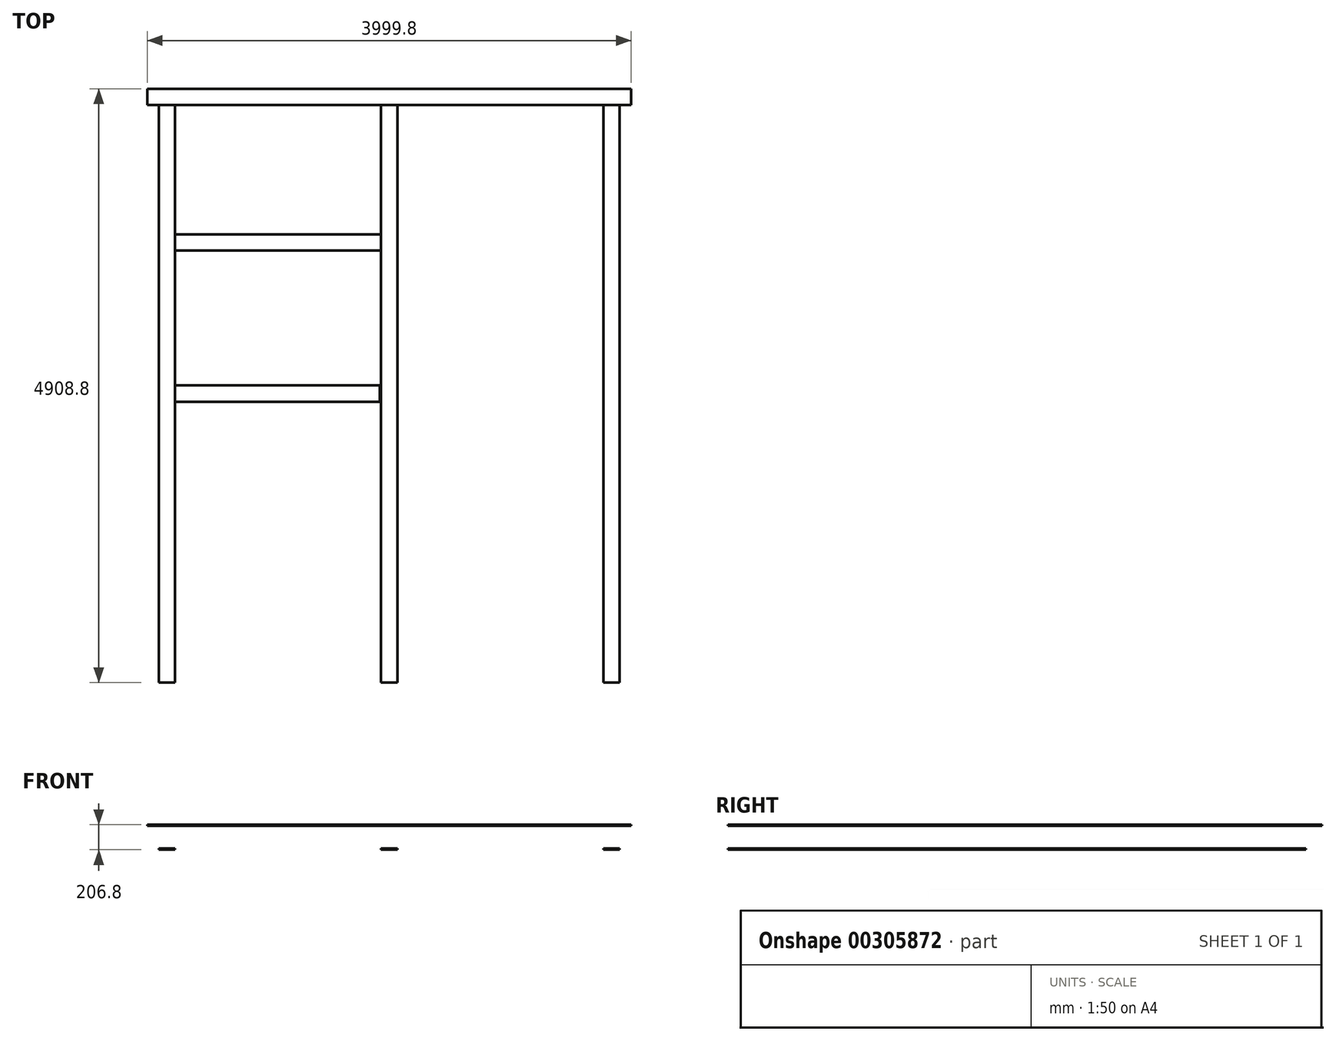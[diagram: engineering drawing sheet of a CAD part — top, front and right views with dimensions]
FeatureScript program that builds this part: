
annotation { "Feature Type Name" : "Feature", "Feature Type Description" : "" }
export const myFeature = defineFeature(function(context is Context, id is Id, definition is map)
    precondition{}
    {
        {
            var Q0;
            Q0=qCreatedBy(makeId("Front.planeOp"),FACE);
            var sketch = newSketch(context, id + "F0", { "sketchPlane" : qUnion([Q0])});
            skLineSegment(sketch, "E0", {"start": v(-1803, 76.08) * mm, "end": v(1869, 76.08) * mm, "construction": true});
            skLineSegment(sketch, "E1", {"start": v(33, 76.08) * mm, "end": v(33, -634.44) * mm, "construction": true});
            skLineSegment(sketch, "E2", {"start": v(-1803, 80.88) * mm, "end": v(1869, 80.88) * mm, "construction": true});
            skLineSegment(sketch, "E3", {"start": v(-1803, 278.08) * mm, "end": v(1869, 278.08) * mm, "construction": true});
            skLineSegment(sketch, "E4", {"start": v(-1803, 282.88) * mm, "end": v(1869, 282.88) * mm, "construction": true});
            skLineSegment(sketch, "E5", {"start": v(-1803, 282.88) * mm, "end": v(-1803, 76.08) * mm, "construction": true});
            skLineSegment(sketch, "E6", {"start": v(-1803, 179.48) * mm, "end": v(1869, 179.48) * mm, "construction": true});
            skLineSegment(sketch, "E7.bottom", {"start": v(-1869.9, 282.88) * mm, "end": v(-1736.1, 282.88) * mm});
            skLineSegment(sketch, "E7.top", {"start": v(-1869.9, 273.28) * mm, "end": v(-1736.1, 273.28) * mm});
            skLineSegment(sketch, "E7.left", {"start": v(-1869.9, 282.88) * mm, "end": v(-1869.9, 273.28) * mm});
            skLineSegment(sketch, "E7.right", {"start": v(-1736.1, 282.88) * mm, "end": v(-1736.1, 273.28) * mm});
            skPoint(sketch, "E7.middle", {"position": v(-1803, 278.08) * mm});
            skLineSegment(sketch, "E8.bottom", {"start": v(-1736.1, 76.08) * mm, "end": v(-1869.9, 76.08) * mm});
            skLineSegment(sketch, "E8.top", {"start": v(-1736.1, 85.68) * mm, "end": v(-1869.9, 85.68) * mm});
            skLineSegment(sketch, "E8.left", {"start": v(-1736.1, 76.08) * mm, "end": v(-1736.1, 85.68) * mm});
            skLineSegment(sketch, "E8.right", {"start": v(-1869.9, 76.08) * mm, "end": v(-1869.9, 85.68) * mm});
            skPoint(sketch, "E8.middle", {"position": v(-1803, 80.88) * mm});
            skLineSegment(sketch, "E9.bottom", {"start": v(-1799.85, 85.68) * mm, "end": v(-1806.15, 85.68) * mm});
            skLineSegment(sketch, "E9.top", {"start": v(-1799.85, 273.28) * mm, "end": v(-1806.15, 273.28) * mm});
            skLineSegment(sketch, "E9.left", {"start": v(-1799.85, 85.68) * mm, "end": v(-1799.85, 273.28) * mm});
            skLineSegment(sketch, "E9.right", {"start": v(-1806.15, 85.68) * mm, "end": v(-1806.15, 273.28) * mm});
            skPoint(sketch, "E9.middle", {"position": v(-1803, 179.48) * mm});
            skLineSegment(sketch, "E10.bottom", {"start": v(99.9, 76.08) * mm, "end": v(-33.9, 76.08) * mm});
            skLineSegment(sketch, "E10.top", {"start": v(99.9, 85.68) * mm, "end": v(-33.9, 85.68) * mm});
            skLineSegment(sketch, "E10.left", {"start": v(99.9, 76.08) * mm, "end": v(99.9, 85.68) * mm});
            skLineSegment(sketch, "E10.right", {"start": v(-33.9, 76.08) * mm, "end": v(-33.9, 85.68) * mm});
            skPoint(sketch, "E10.middle", {"position": v(33, 80.88) * mm});
            skLineSegment(sketch, "E11", {"start": v(33, 76.08) * mm, "end": v(33, 282.88) * mm, "construction": true});
            skLineSegment(sketch, "E12", {"start": v(1869, 282.88) * mm, "end": v(1869, 76.08) * mm, "construction": true});
            skLineSegment(sketch, "E13.bottom", {"start": v(99.9, 282.88) * mm, "end": v(-33.9, 282.88) * mm});
            skLineSegment(sketch, "E13.top", {"start": v(99.9, 273.28) * mm, "end": v(-33.9, 273.28) * mm});
            skLineSegment(sketch, "E13.left", {"start": v(99.9, 282.88) * mm, "end": v(99.9, 273.28) * mm});
            skLineSegment(sketch, "E13.right", {"start": v(-33.9, 282.88) * mm, "end": v(-33.9, 273.28) * mm});
            skPoint(sketch, "E13.middle", {"position": v(33, 278.08) * mm});
            skLineSegment(sketch, "E14.bottom", {"start": v(36.15, 85.68) * mm, "end": v(29.85, 85.68) * mm});
            skLineSegment(sketch, "E14.top", {"start": v(36.15, 273.28) * mm, "end": v(29.85, 273.28) * mm});
            skLineSegment(sketch, "E14.left", {"start": v(36.15, 85.68) * mm, "end": v(36.15, 273.28) * mm});
            skLineSegment(sketch, "E14.right", {"start": v(29.85, 85.68) * mm, "end": v(29.85, 273.28) * mm});
            skPoint(sketch, "E14.middle", {"position": v(33, 179.48) * mm});
            skLineSegment(sketch, "E15.bottom", {"start": v(1802.1, 282.88) * mm, "end": v(1935.9, 282.88) * mm});
            skLineSegment(sketch, "E15.top", {"start": v(1802.1, 273.28) * mm, "end": v(1935.9, 273.28) * mm});
            skLineSegment(sketch, "E15.left", {"start": v(1802.1, 282.88) * mm, "end": v(1802.1, 273.28) * mm});
            skLineSegment(sketch, "E15.right", {"start": v(1935.9, 282.88) * mm, "end": v(1935.9, 273.28) * mm});
            skPoint(sketch, "E15.middle", {"position": v(1869, 278.08) * mm});
            skLineSegment(sketch, "E16.bottom", {"start": v(1935.9, 76.08) * mm, "end": v(1802.1, 76.08) * mm});
            skLineSegment(sketch, "E16.top", {"start": v(1935.9, 85.68) * mm, "end": v(1802.1, 85.68) * mm});
            skLineSegment(sketch, "E16.left", {"start": v(1935.9, 76.08) * mm, "end": v(1935.9, 85.68) * mm});
            skLineSegment(sketch, "E16.right", {"start": v(1802.1, 76.08) * mm, "end": v(1802.1, 85.68) * mm});
            skPoint(sketch, "E16.middle", {"position": v(1869, 80.88) * mm});
            skLineSegment(sketch, "E17.bottom", {"start": v(1872.15, 85.68) * mm, "end": v(1865.85, 85.68) * mm});
            skLineSegment(sketch, "E17.top", {"start": v(1872.15, 273.28) * mm, "end": v(1865.85, 273.28) * mm});
            skLineSegment(sketch, "E17.left", {"start": v(1872.15, 85.68) * mm, "end": v(1872.15, 273.28) * mm});
            skLineSegment(sketch, "E17.right", {"start": v(1865.85, 85.68) * mm, "end": v(1865.85, 273.28) * mm});
            skPoint(sketch, "E17.middle", {"position": v(1869, 179.48) * mm});
            skSolve(sketch);
        }
        {
            var Q0;
            Q0=makeQuery(id+"F0.imprint","IMPRINT",FACE,{"disambiguationData":[TD([[makeQuery(id+"F0.imprint","IMPRINT",EDGE,{"derivedFrom":sQuery(id+"F0.wireOp",EDGE,"E7.bottom")}),-1.0]])]});
            var Q1;
            Q1=makeQuery(id+"F0.imprint","IMPRINT",FACE,{"disambiguationData":[TD([[makeQuery(id+"F0.imprint","IMPRINT",EDGE,{"derivedFrom":sQuery(id+"F0.wireOp",EDGE,"E9.bottom")}),-1.0]])]});
            var Q2;
            Q2=makeQuery(id+"F0.imprint","IMPRINT",FACE,{"disambiguationData":[TD([[makeQuery(id+"F0.imprint","IMPRINT",EDGE,{"derivedFrom":sQuery(id+"F0.wireOp",EDGE,"E8.bottom")}),-1.0]])]});
            var Q3;
            Q3=makeQuery(id+"F0.imprint","IMPRINT",FACE,{"disambiguationData":[TD([[makeQuery(id+"F0.imprint","IMPRINT",EDGE,{"derivedFrom":sQuery(id+"F0.wireOp",EDGE,"E14.bottom")}),-1.0]])]});
            var Q4;
            Q4=makeQuery(id+"F0.imprint","IMPRINT",FACE,{"disambiguationData":[TD([[makeQuery(id+"F0.imprint","IMPRINT",EDGE,{"derivedFrom":sQuery(id+"F0.wireOp",EDGE,"E10.bottom")}),-1.0]])]});
            var Q5;
            Q5=makeQuery(id+"F0.imprint","IMPRINT",FACE,{"disambiguationData":[TD([[makeQuery(id+"F0.imprint","IMPRINT",EDGE,{"derivedFrom":sQuery(id+"F0.wireOp",EDGE,"E13.bottom")}),1.0]])]});
            var Q6;
            Q6=makeQuery(id+"F0.imprint","IMPRINT",FACE,{"disambiguationData":[TD([[makeQuery(id+"F0.imprint","IMPRINT",EDGE,{"derivedFrom":sQuery(id+"F0.wireOp",EDGE,"E15.bottom")}),-1.0]])]});
            var Q7;
            Q7=makeQuery(id+"F0.imprint","IMPRINT",FACE,{"disambiguationData":[TD([[makeQuery(id+"F0.imprint","IMPRINT",EDGE,{"derivedFrom":sQuery(id+"F0.wireOp",EDGE,"E17.bottom")}),-1.0]])]});
            var Q8;
            Q8=makeQuery(id+"F0.imprint","IMPRINT",FACE,{"disambiguationData":[TD([[makeQuery(id+"F0.imprint","IMPRINT",EDGE,{"derivedFrom":sQuery(id+"F0.wireOp",EDGE,"E16.bottom")}),-1.0]])]});
            extrude(context, id + "F1", {"entities" : qUnion([Q0, Q1, Q2, Q3, Q4, Q5, Q6, Q7, Q8]), "depth" : 4775 * mm});
        }
        {
            var Q0;
            Q0=makeQuery(id+"F1.opExtrude","SWEPT_FACE",FACE,{"disambiguationData":[OSD([sQuery(id+"F0.wireOp",EDGE,"E7.bottom")])]});
            var sketch = newSketch(context, id + "F2", { "sketchPlane" : qUnion([Q0])});
            skLineSegment(sketch, "E18.bottom", {"start": v(-1869.9, 0) * mm, "end": v(1935.9, 0) * mm});
            skLineSegment(sketch, "E18.top", {"start": v(-1869.9, 133.8) * mm, "end": v(1935.9, 133.8) * mm});
            skLineSegment(sketch, "E18.left", {"start": v(-1869.9, 0) * mm, "end": v(-1869.9, 133.8) * mm});
            skLineSegment(sketch, "E18.right", {"start": v(1935.9, 0) * mm, "end": v(1935.9, 133.8) * mm});
            skLineSegment(sketch, "E19.bottom", {"start": v(-1869.9, -4775) * mm, "end": v(1935.6, -4775) * mm});
            skLineSegment(sketch, "E19.top", {"start": v(-1869.9, -4908.8) * mm, "end": v(1935.6, -4908.8) * mm});
            skLineSegment(sketch, "E19.left", {"start": v(-1869.9, -4775) * mm, "end": v(-1869.9, -4908.8) * mm});
            skLineSegment(sketch, "E19.right", {"start": v(1935.6, -4775) * mm, "end": v(1935.6, -4908.8) * mm});
            skLineSegment(sketch, "E20", {"start": v(-1736.1, -2387.5) * mm, "end": v(-33.9, -2387.5) * mm, "construction": true});
            skPoint(sketch, "E20.endSnap0", {"position": v(-1736.1, -2387.5) * mm});
            skLineSegment(sketch, "E21", {"start": v(-33.9, -2387.5) * mm, "end": v(99.9, -2387.5) * mm, "construction": true});
            skLineSegment(sketch, "E22", {"start": v(99.9, -2387.5) * mm, "end": v(1802.1, -2387.5) * mm, "construction": true});
            skLineSegment(sketch, "E23.bottom", {"start": v(-1869.9, 133.8) * mm, "end": v(-1966.9, 133.8) * mm});
            skLineSegment(sketch, "E23.top", {"start": v(-1869.9, 0) * mm, "end": v(-1966.9, 0) * mm});
            skLineSegment(sketch, "E23.left", {"start": v(-1869.9, 133.8) * mm, "end": v(-1869.9, 0) * mm});
            skLineSegment(sketch, "E23.right", {"start": v(-1966.9, 133.8) * mm, "end": v(-1966.9, 0) * mm});
            skLineSegment(sketch, "E24.bottom", {"start": v(1935.9, 133.8) * mm, "end": v(2032.9, 133.8) * mm});
            skLineSegment(sketch, "E24.top", {"start": v(1935.9, 0) * mm, "end": v(2032.9, 0) * mm});
            skLineSegment(sketch, "E24.left", {"start": v(1935.9, 133.8) * mm, "end": v(1935.9, 0) * mm});
            skLineSegment(sketch, "E24.right", {"start": v(2032.9, 133.8) * mm, "end": v(2032.9, 0) * mm});
            skLineSegment(sketch, "E25.bottom", {"start": v(-1736.1, -1070.2) * mm, "end": v(-33.9, -1070.2) * mm});
            skLineSegment(sketch, "E25.top", {"start": v(-1736.1, -1204) * mm, "end": v(-33.9, -1204) * mm});
            skLineSegment(sketch, "E25.left", {"start": v(-1736.1, -1070.2) * mm, "end": v(-1736.1, -1204) * mm});
            skLineSegment(sketch, "E25.right", {"start": v(-33.9, -1070.2) * mm, "end": v(-33.9, -1204) * mm});
            skLineSegment(sketch, "E26.bottom", {"start": v(-1736.1, -2318.2) * mm, "end": v(-45.05, -2318.2) * mm});
            skLineSegment(sketch, "E26.top", {"start": v(-1736.1, -2452) * mm, "end": v(-45.05, -2452) * mm});
            skLineSegment(sketch, "E26.left", {"start": v(-1736.1, -2318.2) * mm, "end": v(-1736.1, -2452) * mm});
            skLineSegment(sketch, "E26.right", {"start": v(-45.05, -2318.2) * mm, "end": v(-45.05, -2452) * mm});
            skSolve(sketch);
        }
        {
            var Q0;
            Q0=makeQuery(id+"F2.imprint","IMPRINT",FACE,{"disambiguationData":[TD([[makeQuery(id+"F2.imprint","IMPRINT",EDGE,{"derivedFrom":sQuery(id+"F2.wireOp",EDGE,"E18.top")}),-1.0]])]});
            var Q1;
            Q1=makeQuery(id+"F2.imprint","IMPRINT",FACE,{"disambiguationData":[TD([[makeQuery(id+"F2.imprint","IMPRINT",EDGE,{"derivedFrom":sQuery(id+"F2.wireOp",EDGE,"E23.bottom")}),1.0]])]});
            var Q2;
            Q2=makeQuery(id+"F2.imprint","IMPRINT",FACE,{"disambiguationData":[TD([[makeQuery(id+"F2.imprint","IMPRINT",EDGE,{"derivedFrom":sQuery(id+"F2.wireOp",EDGE,"E24.bottom")}),-1.0]])]});
            var Q3;
            Q3=makeQuery(id+"F2.imprint","IMPRINT",FACE,{"disambiguationData":[TD([[makeQuery(id+"F2.imprint","IMPRINT",EDGE,{"derivedFrom":sQuery(id+"F2.wireOp",EDGE,"E25.bottom")}),-1.0]])]});
            var Q4;
            Q4=makeQuery(id+"F2.imprint","IMPRINT",FACE,{"disambiguationData":[TD([[makeQuery(id+"F2.imprint","IMPRINT",EDGE,{"derivedFrom":sQuery(id+"F2.wireOp",EDGE,"E26.bottom")}),-1.0]])]});
            extrude(context, id + "F3", {"entities" : qUnion([Q0, Q1, Q2, Q3, Q4]), "depth" : -9.6 * mm});
        }
    });
